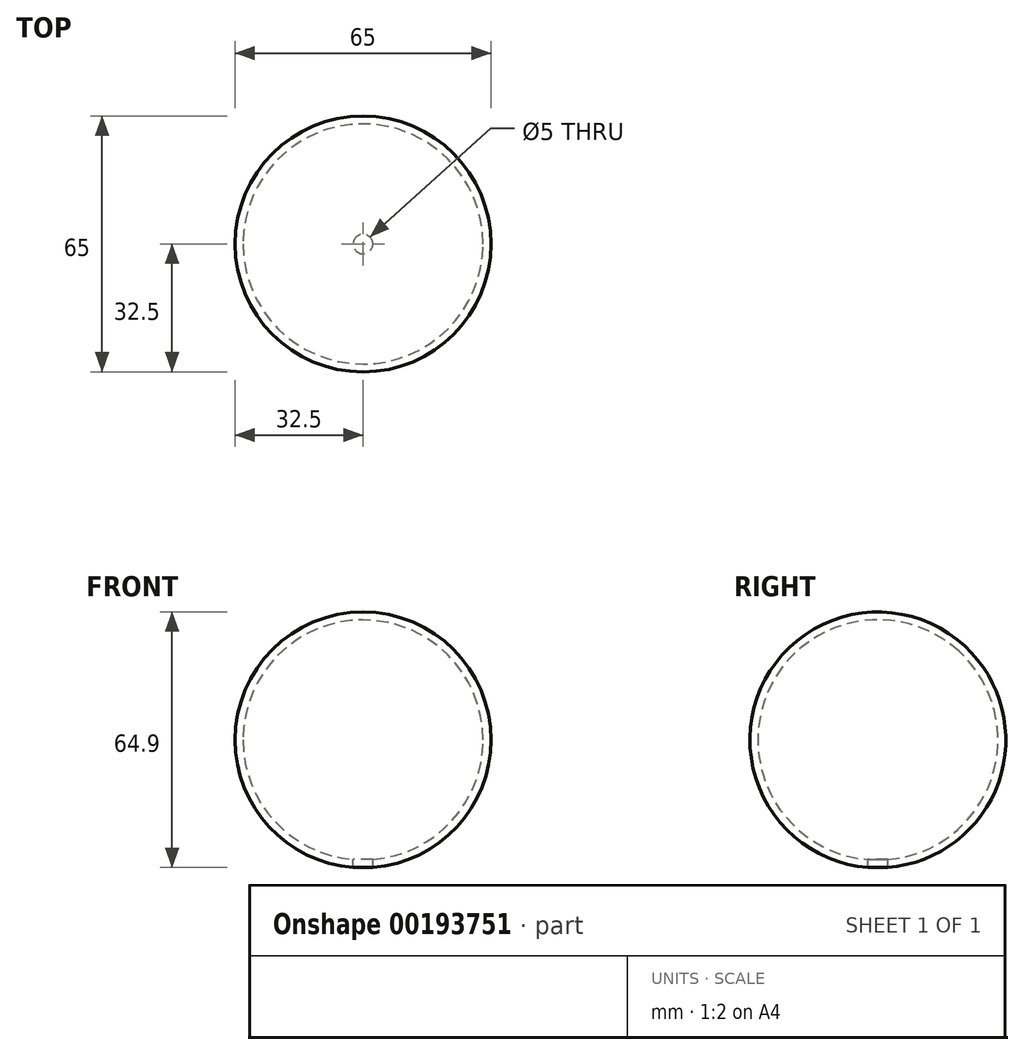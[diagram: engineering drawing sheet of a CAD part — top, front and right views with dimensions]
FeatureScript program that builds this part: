
annotation { "Feature Type Name" : "Feature", "Feature Type Description" : "" }
export const myFeature = defineFeature(function(context is Context, id is Id, definition is map)
    precondition{}
    {
        {
            var Q0;
            Q0=qCreatedBy(makeId("Top.planeOp"),FACE);
            var sketch = newSketch(context, id + "F0", { "sketchPlane" : qUnion([Q0])});
            skLineSegment(sketch, "E0", {"start": v(-32.5, 0) * mm, "end": v(32.5, 0) * mm});
            skArc(sketch, "E1", {"start": v(-32.5, 0) * mm, "mid": v(0, 32.5) * mm, "end": v(32.5, 0) * mm});
            skSolve(sketch);
        }
        {
            var Q0;
            Q0 = qSketchRegion(id + "F0", true);
            var Q1;
            Q1=sQuery(id+"F0.wireOp",EDGE,"E0");
            revolve(context, id + "F1", {"entities" : qUnion([Q0]), "axis" : qUnion([Q1]), "revolveType" : RevolveType.FULL});
        }
        {
            var Q0;
            Q0=makeQuery(id+"F1.opRevolve","SWEPT_BODY",BODY,{"disambiguationData":[OSD([sQuery(id+"F0.wireOp",EDGE,"E0"),sQuery(id+"F0.wireOp",EDGE,"E1")])]});
            var Q1;
            Q1=makeQuery(id+"F1.opRevolve","SWEPT_FACE",FACE,{"disambiguationData":[OSD([sQuery(id+"F0.wireOp",EDGE,"E1")])]});
            var Q2;
            Q2=makeQuery(id+"F1.opRevolve","SWEPT_BODY",BODY,{"disambiguationData":[OSD([sQuery(id+"F0.wireOp",EDGE,"E0"),sQuery(id+"F0.wireOp",EDGE,"E1")])]});
            shell(context, id + "F2", {"isHollow" : true, "entities" : qUnion([Q0, Q1]), "parts" : qUnion([Q2]), "thickness" : 2 * mm});
        }
        {
            var Q0;
            Q0=qCreatedBy(makeId("Top.planeOp"),FACE);
            var sketch = newSketch(context, id + "F3", { "sketchPlane" : qUnion([Q0])});
            skCircle(sketch, "E2", {"center": v(0, 0) * mm, "radius": 2.5 * mm});
            skSolve(sketch);
        }
        {
            var Q0;
            Q0 = qSketchRegion(id + "F3", true);
            extrude(context, id + "F4", {"entities" : qUnion([Q0]), "operationType" : NewBodyOperationType.REMOVE, "endBound" : BoundingType.THROUGH_ALL, "oppositeDirection" : true, "depth" : 25 * mm});
        }
    });
